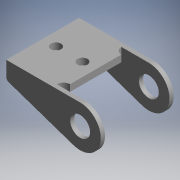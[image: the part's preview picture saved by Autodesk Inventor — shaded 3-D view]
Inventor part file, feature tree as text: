
AUTODESK INVENTOR PART (.ipt)
format: ipt  version: 2017.3 (Build 213256000, 256)  size: 139,264 bytes
history: native  units: mm (DEFAULTED — no unit token found)
features: other x21, extrude x3, sketch x3
ambient origin geometry x8: Origin, YZ Plane, XZ Plane, XY Plane, X Axis, Y Axis, Z Axis, Center Point
bodies: Solid1 (feature_tree)
feature tree (27):
  extrude  "Extrusion1"  Depth=1.25mm TaperAngle=0.0deg
  extrude  "Extrusion2"  TaperAngle=0.0deg  [1 undecoded]
  extrude  "Extrusion3"  [1 undecoded]
  other  "end_2_XY"
  other  "end_2_YZ"
  other  "end_2_ZX"
  other  "end_2_X"
  other  "end_2_Y"
  other  "end_2_Z"
  other  "end_2_Center"
  other  "end_move_XY"
  other  "end_move_YZ"
  other  "end_move_ZX"
  other  "end_move_X"
  other  "end_move_Y"
  other  "end_move_Z"
  other  "end_move_Center"
  other  "to_dummy_XY"
  other  "to_dummy_YZ"
  other  "to_dummy_ZX"
  other  "to_dummy_X"
  other  "to_dummy_Y"
  other  "to_dummy_Z"
  other  "to_dummy_Center"
  sketch  "Sketch_45"  dims[d0=2.0mm d1=0.0mm d2=1.25mm d3=0.0mm]
  sketch  "Sketch_47"  dims[d4=1.25mm d5=0.0mm d6=0.0mm]
  sketch  "Sketch_76"
note: 2 required parameter values undecoded (feature->parameter linkage not recoverable at this tier; creation-order binding heuristic only, values carry confidence <= 0.55)
